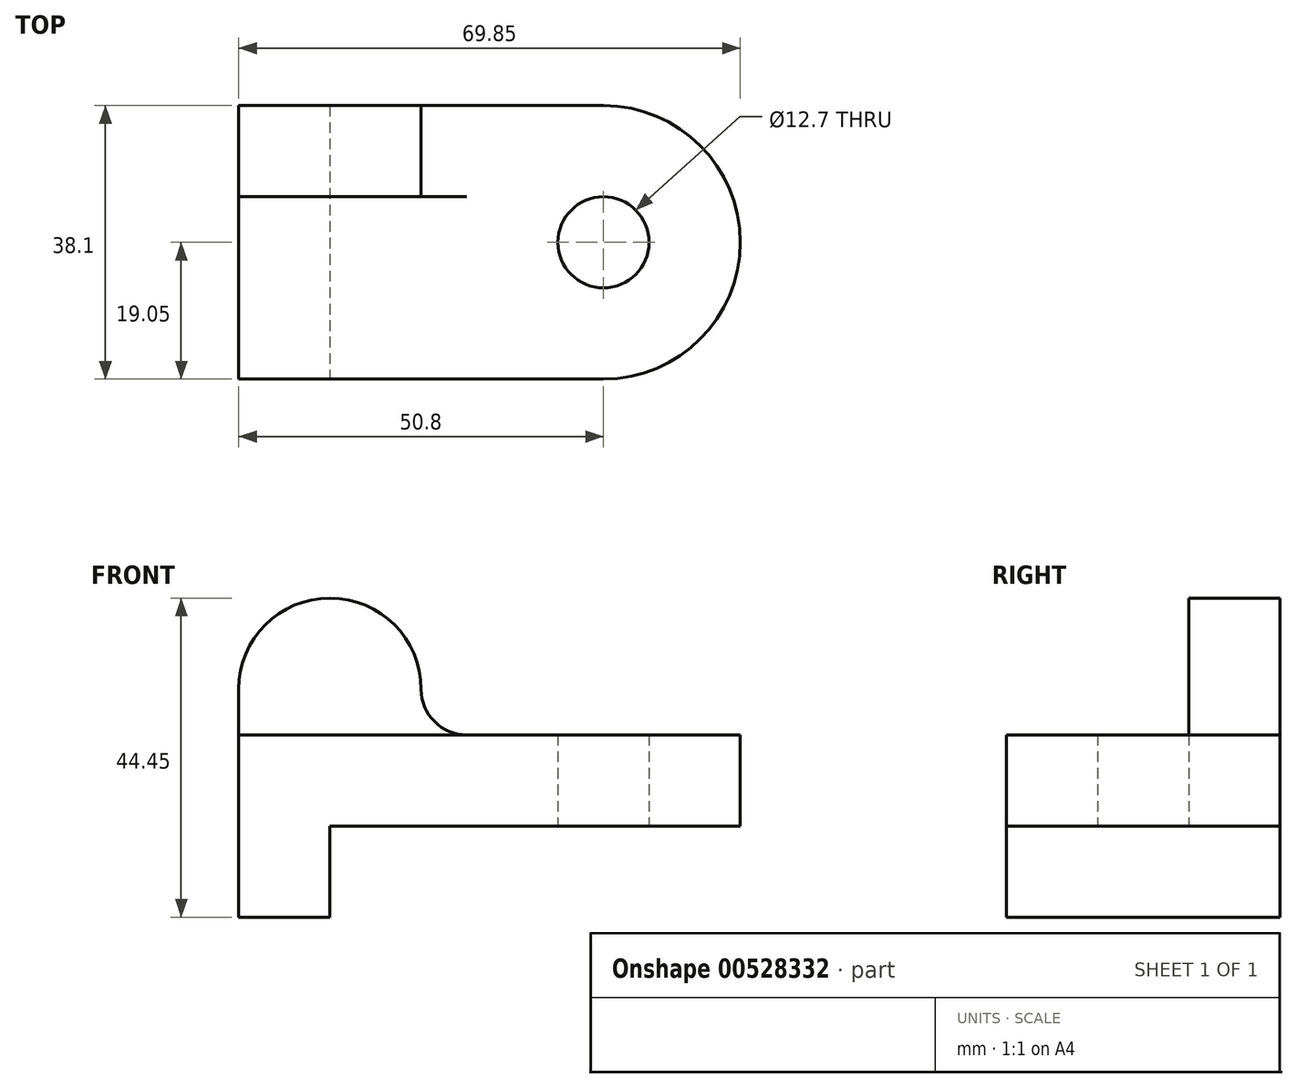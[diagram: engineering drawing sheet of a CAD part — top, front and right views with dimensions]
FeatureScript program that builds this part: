
annotation { "Feature Type Name" : "Feature", "Feature Type Description" : "" }
export const myFeature = defineFeature(function(context is Context, id is Id, definition is map)
    precondition{}
    {
        {
            var Q0;
            Q0=qCreatedBy(makeId("Top.planeOp"),FACE);
            var sketch = newSketch(context, id + "F0", { "sketchPlane" : qUnion([Q0])});
            skLineSegment(sketch, "E0", {"start": v(0, 0) * mm, "end": v(0, -38.1) * mm});
            skLineSegment(sketch, "E1", {"start": v(0, -38.1) * mm, "end": v(-12.7, -38.1) * mm});
            skLineSegment(sketch, "E2", {"start": v(-12.7, -38.1) * mm, "end": v(-12.7, 0) * mm});
            skLineSegment(sketch, "E3", {"start": v(-12.7, 0) * mm, "end": v(0, 0) * mm});
            skLineSegment(sketch, "E4", {"start": v(0, 0) * mm, "end": v(38.1, 0) * mm});
            skLineSegment(sketch, "E5", {"start": v(38.1, 0) * mm, "end": v(38.1, -38.1) * mm, "construction": true});
            skLineSegment(sketch, "E6", {"start": v(38.1, -38.1) * mm, "end": v(0, -38.1) * mm});
            skArc(sketch, "E7", {"start": v(38.1, -38.1) * mm, "mid": v(57.15, -19.05) * mm, "end": v(38.1, 0) * mm});
            skCircle(sketch, "E8", {"center": v(38.1, -19.05) * mm, "radius": 6.35 * mm});
            skSolve(sketch);
        }
        {
            var Q0;
            Q0=makeQuery(id+"F0.imprint","IMPRINT",FACE,{"disambiguationData":[TD([[makeQuery(id+"F0.imprint","IMPRINT",EDGE,{"derivedFrom":sQuery(id+"F0.wireOp",EDGE,"E0")}),1.0]])]});
            var Q1;
            Q1=makeQuery(id+"F0.imprint","IMPRINT",FACE,{"disambiguationData":[TD([[makeQuery(id+"F0.imprint","IMPRINT",EDGE,{"derivedFrom":sQuery(id+"F0.wireOp",EDGE,"E0")}),-1.0]])]});
            extrude(context, id + "F1", {"entities" : qUnion([Q0, Q1]), "depth" : 12.7 * mm, "offsetDistance" : 25.4 * mm});
        }
        {
            var Q0;
            Q0=makeQuery(id+"F0.imprint","IMPRINT",FACE,{"disambiguationData":[TD([[makeQuery(id+"F0.imprint","IMPRINT",EDGE,{"derivedFrom":sQuery(id+"F0.wireOp",EDGE,"E0")}),-1.0]])]});
            extrude(context, id + "F2", {"entities" : qUnion([Q0]), "operationType" : NewBodyOperationType.ADD, "oppositeDirection" : true, "depth" : 12.7 * mm, "offsetDistance" : 25.4 * mm});
        }
        {
            var Q0;
            {var subQ0=sQuery(id+"F0.wireOp",EDGE,"E3");Q0=makeQuery(id+"F2.boolean.opBoolean","MERGE",FACE,{"derivedFrom":[makeQuery(id+"F1.opExtrude","SWEPT_FACE",FACE,{"disambiguationData":[OSD([subQ0,sQuery(id+"F0.wireOp",EDGE,"E4")])]}),makeQuery(id+"F2.opExtrude","SWEPT_FACE",FACE,{"disambiguationData":[OSD([subQ0])]})]});}
            var sketch = newSketch(context, id + "F3", { "sketchPlane" : qUnion([Q0])});
            skLineSegment(sketch, "E9", {"start": v(12.7, 12.7) * mm, "end": v(-19.05, 12.7) * mm});
            skLineSegment(sketch, "E10", {"start": v(12.7, 12.7) * mm, "end": v(12.7, 19.05) * mm});
            skLineSegment(sketch, "E11", {"start": v(12.7, 19.05) * mm, "end": v(-12.7, 19.05) * mm, "construction": true});
            skArc(sketch, "E12", {"start": v(-19.05, 12.7) * mm, "mid": v(-14.56, 14.56) * mm, "end": v(-12.7, 19.05) * mm});
            skArc(sketch, "E13", {"start": v(12.7, 19.05) * mm, "mid": v(0, 31.75) * mm, "end": v(-12.7, 19.05) * mm});
            skSolve(sketch);
        }
        {
            var Q0;
            Q0=makeQuery(id+"F3.imprint","IMPRINT",FACE,{"disambiguationData":[TD([[makeQuery(id+"F3.imprint","IMPRINT",EDGE,{"derivedFrom":sQuery(id+"F3.wireOp",EDGE,"JOEfs0Jr-dr2d-WYfC-P4wC-IsICSyyLL72S")}),-1.0]])]});
            var Q1;
            Q1=makeQuery(id+"F3.imprint","IMPRINT",FACE,{"disambiguationData":[TD([[makeQuery(id+"F3.imprint","IMPRINT",EDGE,{"derivedFrom":sQuery(id+"F3.wireOp",EDGE,"E9")}),-1.0]])]});
            extrude(context, id + "F4", {"entities" : qUnion([Q0, Q1]), "operationType" : NewBodyOperationType.ADD, "oppositeDirection" : true, "depth" : 12.7 * mm, "offsetDistance" : 25.4 * mm});
        }
    });
